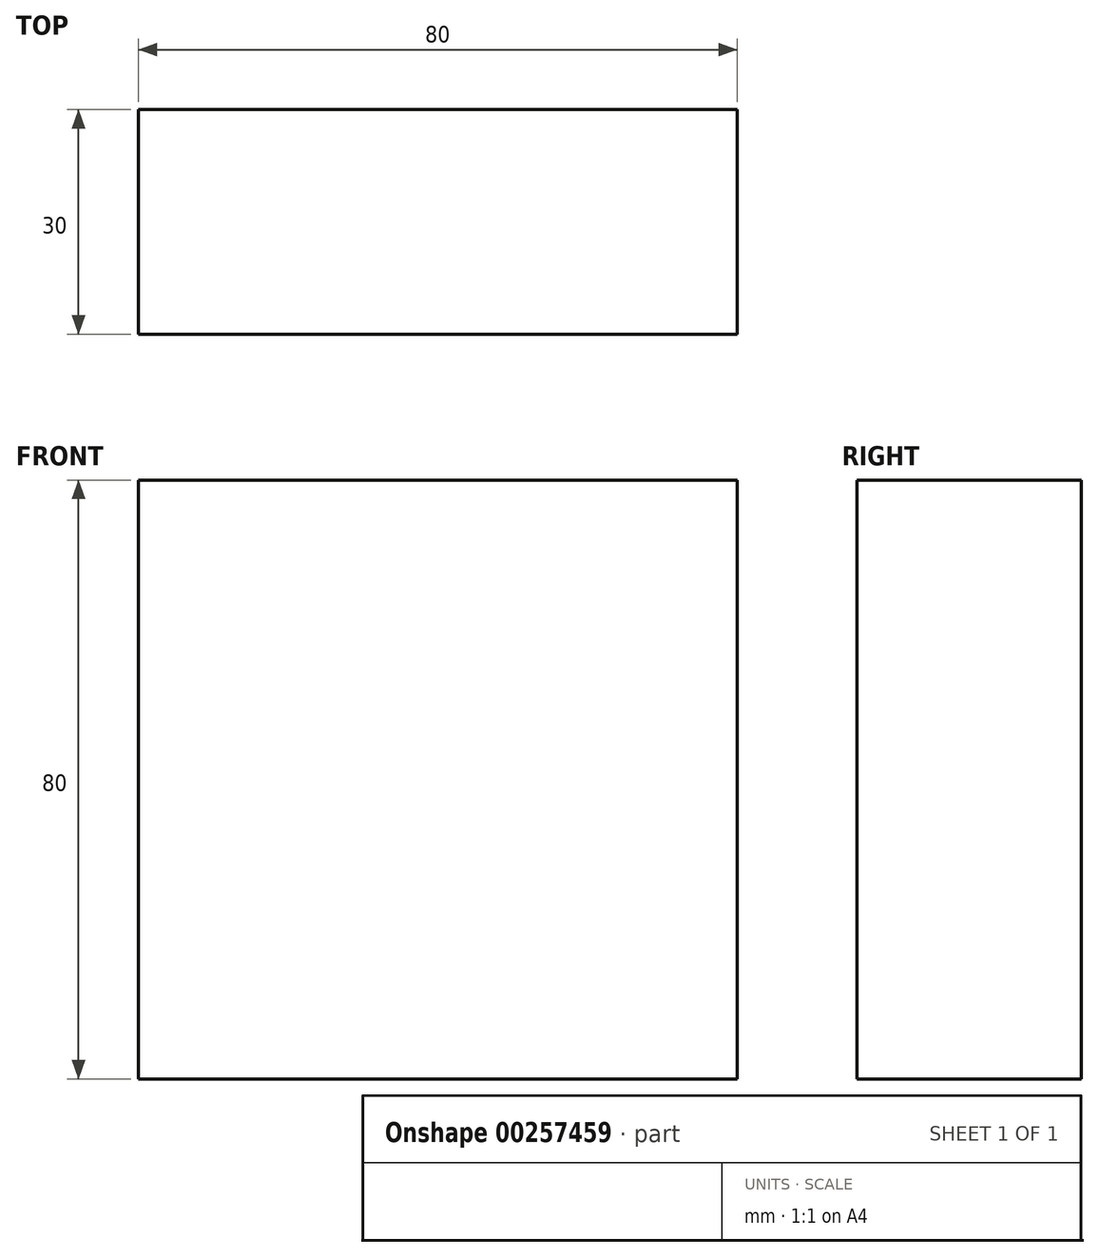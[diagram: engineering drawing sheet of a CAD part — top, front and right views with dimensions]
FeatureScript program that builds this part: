
annotation { "Feature Type Name" : "Feature", "Feature Type Description" : "" }
export const myFeature = defineFeature(function(context is Context, id is Id, definition is map)
    precondition{}
    {
        {
            var Q0;
            Q0=qCreatedBy(makeId("Front.planeOp"),FACE);
            var sketch = newSketch(context, id + "F0", { "sketchPlane" : qUnion([Q0])});
            skLineSegment(sketch, "E0.bottom", {"start": v(-40, 40) * mm, "end": v(40, 40) * mm});
            skLineSegment(sketch, "E0.top", {"start": v(-40, -40) * mm, "end": v(40, -40) * mm});
            skLineSegment(sketch, "E0.left", {"start": v(-40, 40) * mm, "end": v(-40, -40) * mm});
            skLineSegment(sketch, "E0.right", {"start": v(40, 40) * mm, "end": v(40, -40) * mm});
            skPoint(sketch, "E0.middle", {"position": v(0, 0) * mm});
            skPoint(sketch, "E1", {"position": v(-40, -20) * mm});
            skPoint(sketch, "E2", {"position": v(-40, 20) * mm});
            skLineSegment(sketch, "E3", {"start": v(-40, 20) * mm, "end": v(-18.66, 20) * mm});
            skPoint(sketch, "E4", {"position": v(10, -40) * mm});
            skLineSegment(sketch, "E5", {"start": v(10, -40) * mm, "end": v(10, -1.13) * mm});
            skPoint(sketch, "E6", {"position": v(-10, -40) * mm});
            skArc(sketch, "E7", {"start": v(-10, -40) * mm, "mid": v(-22.62, -26.43) * mm, "end": v(-40, -20) * mm});
            skArc(sketch, "E8", {"start": v(10, -1.13) * mm, "mid": v(-0.86, 14.15) * mm, "end": v(-18.66, 20) * mm});
            skSolve(sketch);
        }
        {
            var Q0;
            {var subQ2=sQuery(id+"F0.wireOp",EDGE,"E0.bottom");Q0=makeQuery(id+"F0.imprint","IMPRINT",FACE,{"disambiguationData":[TD([[makeQuery(id+"F0.imprint","IMPRINT",EDGE,{"derivedFrom":subQ2}),-1.0]])]});}
            var Q1;
            {var subQ3=sQuery(id+"F0.wireOp",EDGE,"E3");Q1=makeQuery(id+"F0.imprint","IMPRINT",FACE,{"disambiguationData":[TD([[makeQuery(id+"F0.imprint","IMPRINT",EDGE,{"derivedFrom":subQ3}),-1.0]])]});}
            var Q2;
            {var subQ3=sQuery(id+"F0.wireOp",EDGE,"E7");Q2=makeQuery(id+"F0.imprint","IMPRINT",FACE,{"disambiguationData":[TD([[makeQuery(id+"F0.imprint","IMPRINT",EDGE,{"derivedFrom":subQ3}),1.0]])]});}
            extrude(context, id + "F1", {"entities" : qUnion([Q0, Q1, Q2]), "oppositeDirection" : true, "depth" : 30 * mm});
        }
    });
